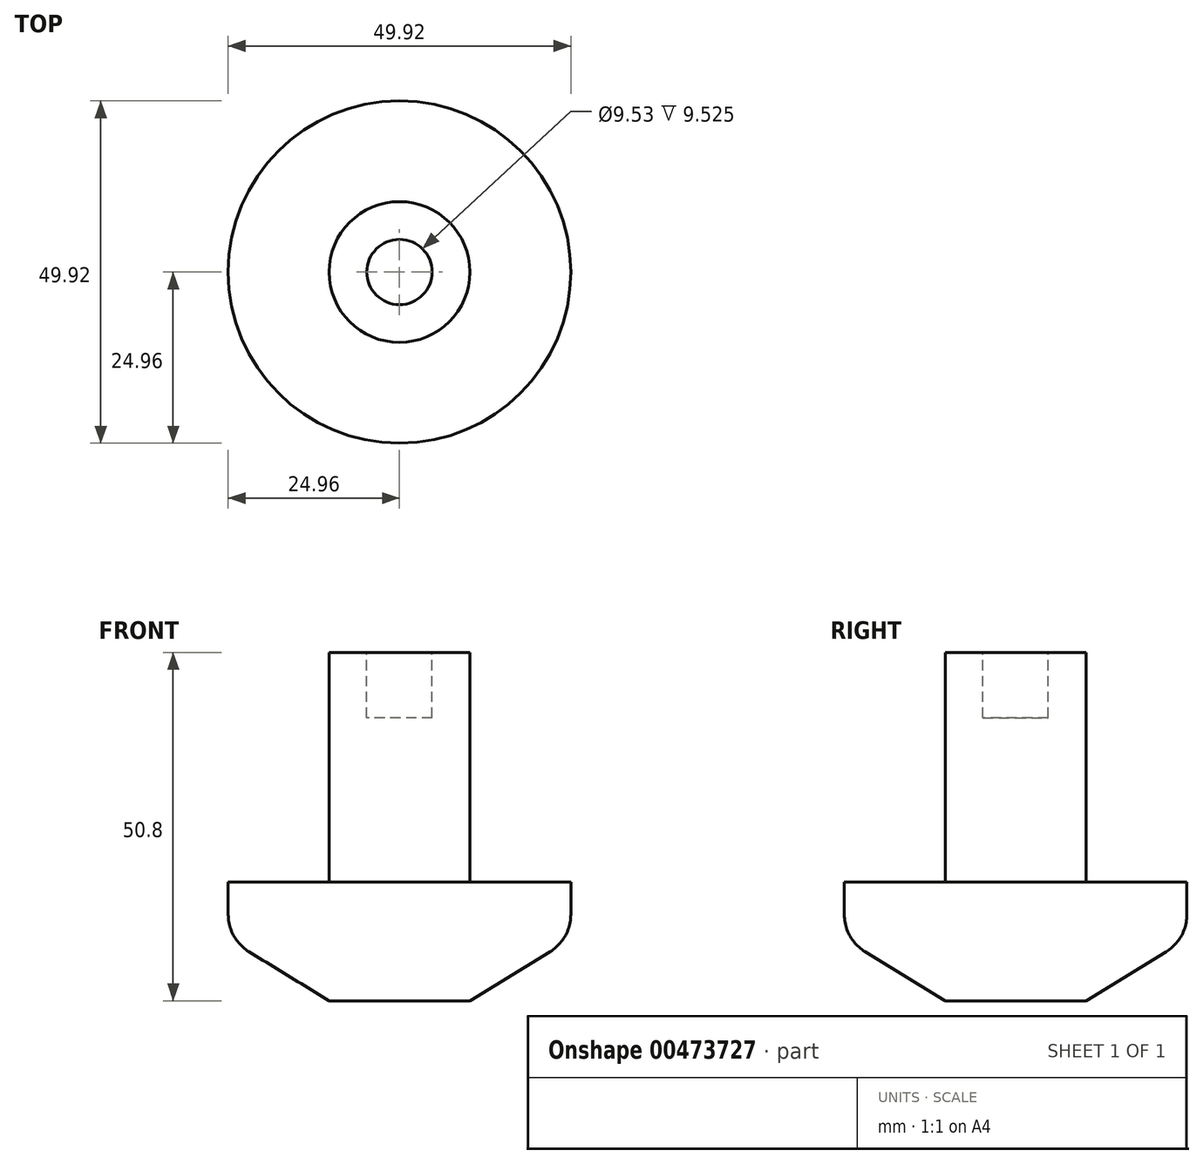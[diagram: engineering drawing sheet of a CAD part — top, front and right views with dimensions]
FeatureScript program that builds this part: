
annotation { "Feature Type Name" : "Feature", "Feature Type Description" : "" }
export const myFeature = defineFeature(function(context is Context, id is Id, definition is map)
    precondition{}
    {
        {
            var Q0;
            Q0=qCreatedBy(makeId("Front.planeOp"),FACE);
            var sketch = newSketch(context, id + "F0", { "sketchPlane" : qUnion([Q0])});
            skLineSegment(sketch, "E0", {"start": v(0, 0) * mm, "end": v(0, 50.8) * mm});
            skLineSegment(sketch, "E1", {"start": v(0, 0) * mm, "end": v(10.26, 0) * mm});
            skLineSegment(sketch, "E2", {"start": v(10.26, 0) * mm, "end": v(21.93, 7.15) * mm});
            skLineSegment(sketch, "E3", {"start": v(24.96, 12.57) * mm, "end": v(24.96, 17.33) * mm});
            skLineSegment(sketch, "E4", {"start": v(24.96, 17.33) * mm, "end": v(10.26, 17.33) * mm});
            skLineSegment(sketch, "E5", {"start": v(10.26, 17.33) * mm, "end": v(10.26, 50.8) * mm});
            skLineSegment(sketch, "E6", {"start": v(10.26, 50.8) * mm, "end": v(0, 50.8) * mm});
            skPoint(sketch, "E7.visualSharp", {"position": v(24.96, 9.01) * mm});
            skArc(sketch, "E7.filletArc", {"start": v(21.93, 7.15) * mm, "mid": v(24.15, 9.47) * mm, "end": v(24.96, 12.57) * mm});
            skSolve(sketch);
        }
        {
            var Q0;
            Q0=makeQuery(id+"F0.imprint","IMPRINT",FACE,{"disambiguationData":[TD([[makeQuery(id+"F0.imprint","IMPRINT",EDGE,{"derivedFrom":sQuery(id+"F0.wireOp",EDGE,"E0")}),-1.0]])]});
            var Q1;
            Q1=sQuery(id+"F0.wireOp",EDGE,"E0");
            revolve(context, id + "F1", {"entities" : qUnion([Q0]), "axis" : qUnion([Q1]), "revolveType" : RevolveType.FULL});
        }
        {
            var Q0;
            Q0=makeQuery(id+"F1.opRevolve","SWEPT_FACE",FACE,{"disambiguationData":[OSD([sQuery(id+"F0.wireOp",EDGE,"E6")])]});
            var sketch = newSketch(context, id + "F2", { "sketchPlane" : qUnion([Q0])});
            skCircle(sketch, "E8", {"center": v(0, 0) * mm, "radius": 4.76 * mm});
            skSolve(sketch);
        }
        {
            var Q0;
            Q0=makeQuery(id+"F2.imprint","IMPRINT",FACE,{"disambiguationData":[TD([[makeQuery(id+"F2.imprint","IMPRINT",EDGE,{"derivedFrom":sQuery(id+"F2.wireOp",EDGE,"E8")}),1.0]])]});
            extrude(context, id + "F3", {"entities" : qUnion([Q0]), "operationType" : NewBodyOperationType.REMOVE, "oppositeDirection" : true, "depth" : 9.52 * mm});
        }
    });
